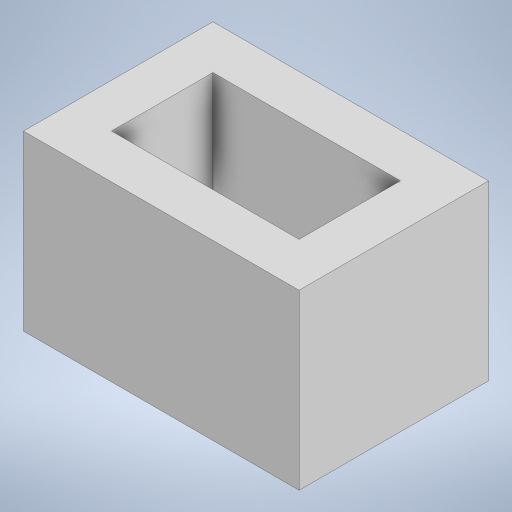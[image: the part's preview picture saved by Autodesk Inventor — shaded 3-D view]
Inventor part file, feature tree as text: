
AUTODESK INVENTOR PART (.ipt)
format: ipt  version: 2023.5 (Build 275446000, 446)  size: 265,216 bytes
history: native  units: in
note: dims shown in document units (in); Inventor stores cm internally (conversion verified against a paired STEP export)
features: extrude x3, sketch x3
ambient origin geometry x8: Origin, YZ Plane, XZ Plane, XY Plane, X Axis, Y Axis, Z Axis, Center Point
bodies: Solid1 (feature_tree)
feature tree (6):
  extrude  "Extrusion1"  Depth=0.2717in
  extrude  "Extrusion2"  Depth=0.1181in
  extrude  "Extrusion3"  Depth=0.1181in
  sketch  "Sketch1"  dims[d0=0.5028in d1=0.2717in]
  sketch  "Sketch2"  dims[d2=0.1181in d3=0.1181in]
  sketch  "Sketch3"  dims[d4=0.1181in d5=0.1181in d6=0.3465in d7=0.0in d8=0.1181in d9=0.0in d10=0.3268in d11=0.1181in d12=0.0in]
